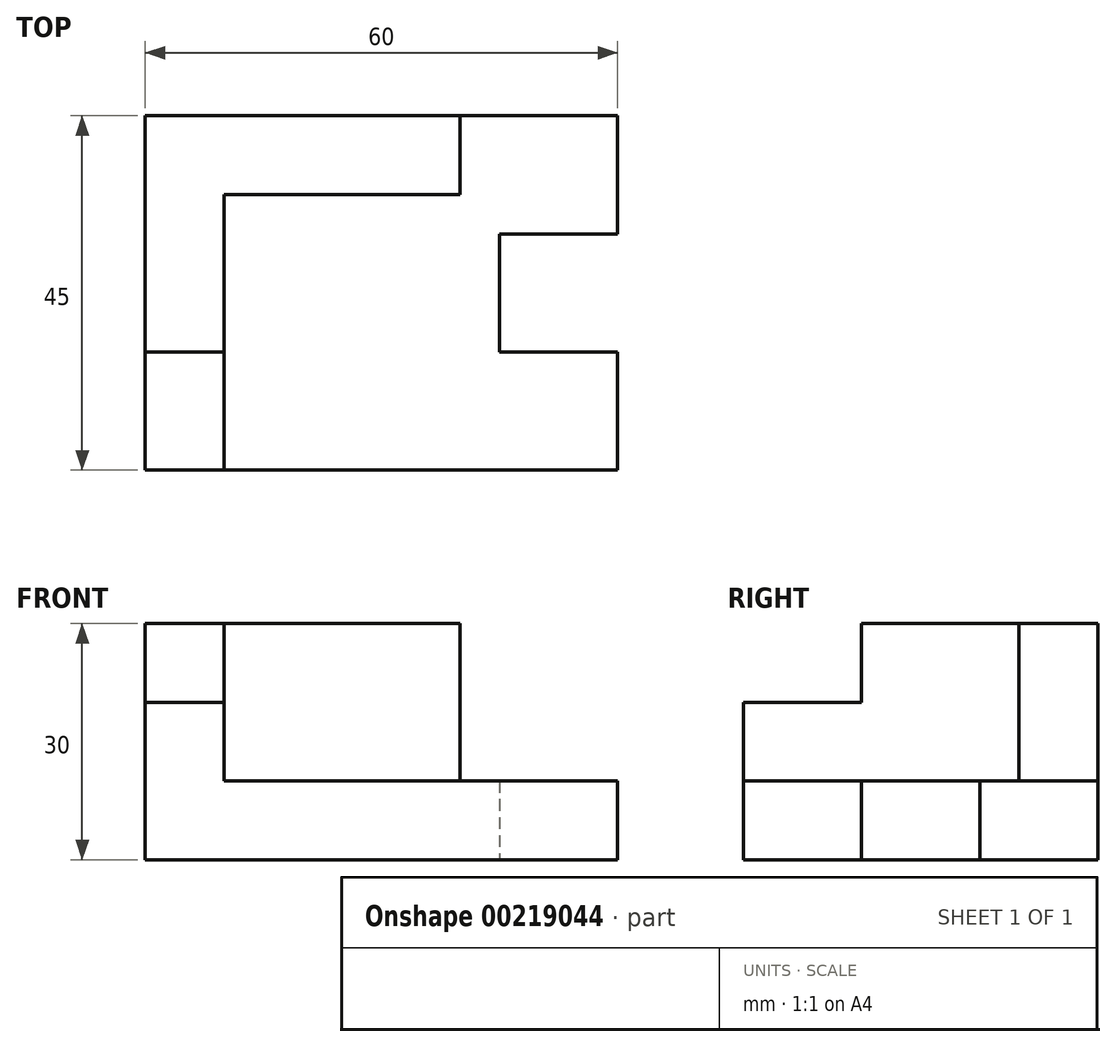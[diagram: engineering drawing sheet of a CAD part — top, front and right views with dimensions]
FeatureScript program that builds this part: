
annotation { "Feature Type Name" : "Feature", "Feature Type Description" : "" }
export const myFeature = defineFeature(function(context is Context, id is Id, definition is map)
    precondition{}
    {
        {
            var Q0;
            Q0=qCreatedBy(makeId("Top.planeOp"),FACE);
            var sketch = newSketch(context, id + "F0", { "sketchPlane" : qUnion([Q0])});
            skLineSegment(sketch, "E0", {"start": v(0, 0) * mm, "end": v(60, 0) * mm});
            skLineSegment(sketch, "E1", {"start": v(60, 0) * mm, "end": v(60, 15) * mm});
            skLineSegment(sketch, "E2", {"start": v(60, 15) * mm, "end": v(45, 15) * mm});
            skLineSegment(sketch, "E3", {"start": v(45, 15) * mm, "end": v(45, 30) * mm});
            skLineSegment(sketch, "E4", {"start": v(45, 30) * mm, "end": v(60, 30) * mm});
            skLineSegment(sketch, "E5", {"start": v(60, 30) * mm, "end": v(60, 45) * mm});
            skLineSegment(sketch, "E6", {"start": v(60, 45) * mm, "end": v(0, 45) * mm});
            skLineSegment(sketch, "E7", {"start": v(0, 45) * mm, "end": v(0, 0) * mm});
            skLineSegment(sketch, "E8", {"start": v(40, 45) * mm, "end": v(40, 35) * mm});
            skLineSegment(sketch, "E9", {"start": v(40, 35) * mm, "end": v(10, 35) * mm});
            skLineSegment(sketch, "E10", {"start": v(10, 35) * mm, "end": v(10, 0) * mm});
            skLineSegment(sketch, "E11", {"start": v(0, 15) * mm, "end": v(10, 15) * mm});
            skSolve(sketch);
        }
        {
            var Q0;
            {var subQ6=sQuery(id+"F0.wireOp",EDGE,"E1");Q0=makeQuery(id+"F0.imprint","IMPRINT",FACE,{"disambiguationData":[TD([[makeQuery(id+"F0.imprint","IMPRINT",EDGE,{"derivedFrom":subQ6}),1.0]])]});}
            extrude(context, id + "F1", {"entities" : qUnion([Q0]), "depth" : 10 * mm});
        }
        {
            var Q0;
            {var subQ5=sQuery(id+"F0.wireOp",EDGE,"E11");Q0=makeQuery(id+"F0.imprint","IMPRINT",FACE,{"disambiguationData":[TD([[makeQuery(id+"F0.imprint","IMPRINT",EDGE,{"derivedFrom":subQ5}),-1.0]])]});}
            extrude(context, id + "F2", {"entities" : qUnion([Q0]), "operationType" : NewBodyOperationType.ADD, "depth" : 20 * mm});
        }
        {
            var Q0;
            {var subQ1=sQuery(id+"F0.wireOp",EDGE,"E8");Q0=makeQuery(id+"F0.imprint","IMPRINT",FACE,{"disambiguationData":[TD([[makeQuery(id+"F0.imprint","IMPRINT",EDGE,{"derivedFrom":subQ1}),-1.0]])]});}
            extrude(context, id + "F3", {"entities" : qUnion([Q0]), "operationType" : NewBodyOperationType.ADD, "depth" : 30 * mm});
        }
    });
